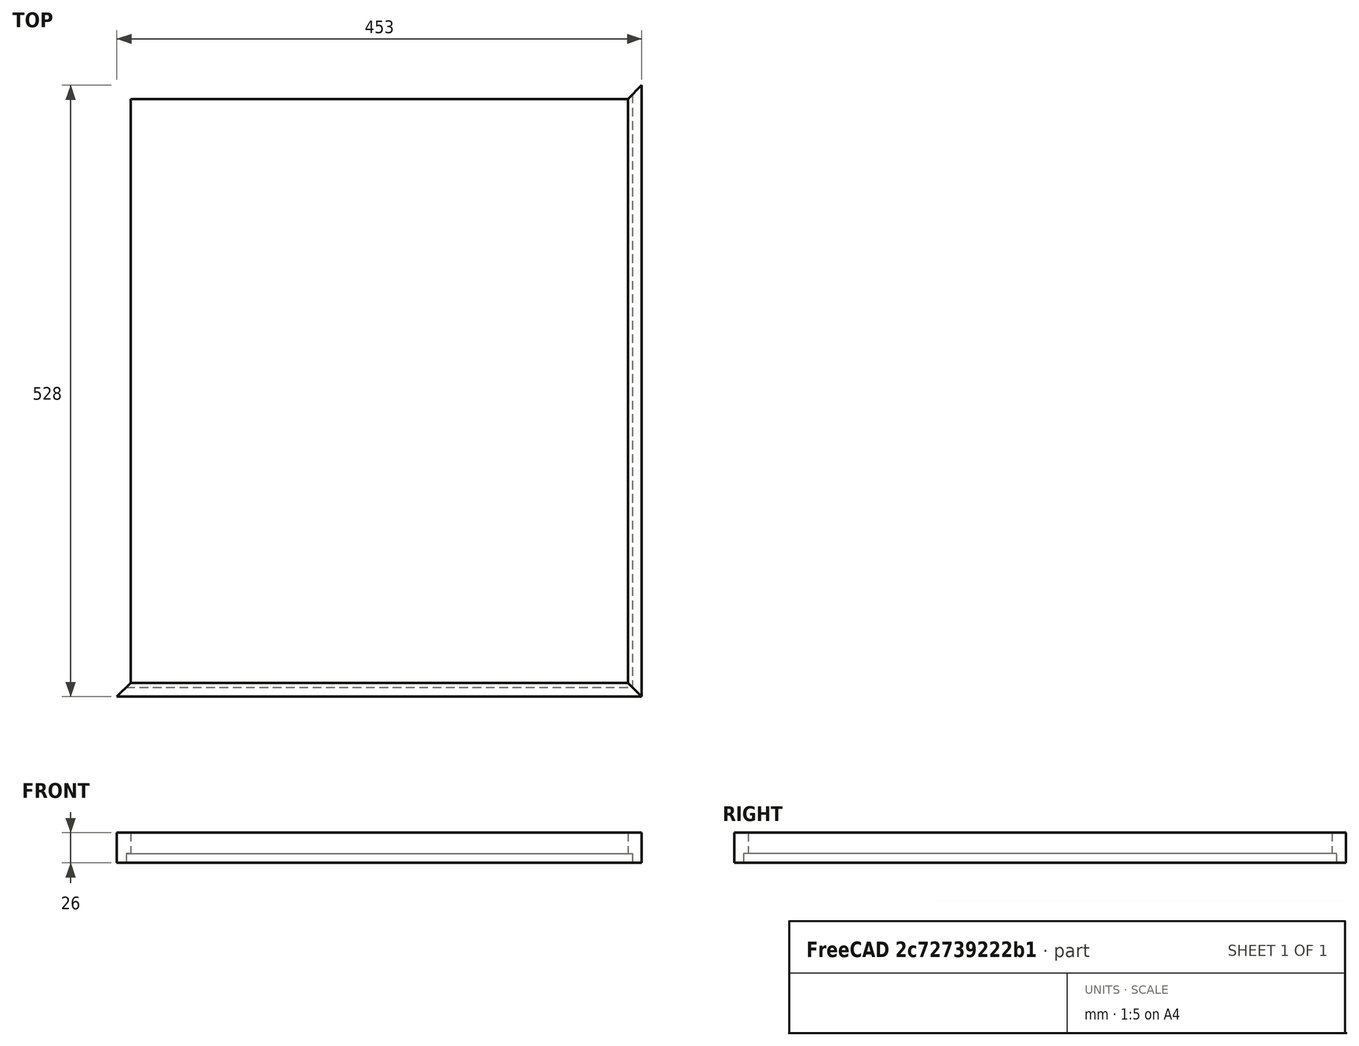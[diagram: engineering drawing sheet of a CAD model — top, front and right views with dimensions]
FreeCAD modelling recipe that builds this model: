
FCSTD DOCUMENT  (FreeCAD 0.19R)
Label: streha
License: All rights reserved
LicenseURL: http://en.wikipedia.org/wiki/All_rights_reserved
objects: Sketcher::SketchObject×8, PartDesign::CoordinateSystem×7, TechDraw::DrawProjGroupItem×6, TechDraw::DrawViewDimension×6, App::Link×5, PartDesign::Pocket×4, App::Part×4, App::DocumentObjectGroup×3, PartDesign::Pad×3, PartDesign::Body×3, TechDraw::DrawProjGroup×3, TechDraw::DrawRichAnno×3, App::FeaturePython×1, TechDraw::DrawSVGTemplate×1, TechDraw::DrawViewPart×1, TechDraw::DrawPage×1
note: 32 computed .brp shape members not serialized (recipe doc carries the construction recipe); baked Part::Feature solids carry a one-line shape summary decoded from their .brp

FEATURE [PartDesign::CoordinateSystem] LCS_Origin
  AttacherType = Attacher::AttachEngine3D
  MapMode = 2
  Support = -> [X_Axis]
FEATURE [App::FeaturePython] Variables  # WARN: FeaturePython — macro-defined, semantics opaque (R4)
  Type = App::PropertyContainer
  bottom_thickness = 18
  inner_depth = 450
  inner_width = 375
  wall_thickness = 27
FEATURE [App::DocumentObjectGroup] Constraints
FEATURE [App::DocumentObjectGroup] Configurations
FEATURE [PartDesign::CoordinateSystem] LCS_0004
  AttacherType = Attacher::AttachEngine3D
  MapMode = 2
  Support = -> [X_Axis005]
FEATURE [PartDesign::CoordinateSystem] LCS_0005
  AttacherType = Attacher::AttachEngine3D
  MapMode = 2
  Support = -> [X_Axis006]
FEATURE [Sketcher::SketchObject] Sketch003  label="Sketch004"
  FullyConstrained = true
  MapMode = 5
  Placement = pos=(0,0,0) rot=(1,0,0;1.5708rad)
  Support = -> [XZ_Plane006]
  expr: Constraints[12] = Variables.inner_width / 2 + Variables.wall_thickness
  sketch-geometry (6):
    g0: LineSegment StartX=214.5 StartY=0 StartZ=0 EndX=218.5 EndY=0 EndZ=0
    g1: LineSegment StartX=218.5 StartY=0 StartZ=0 EndX=218.5 EndY=-8 EndZ=0
    g2: LineSegment StartX=218.5 StartY=-8 StartZ=0 EndX=226.5 EndY=-8 EndZ=0
    g3: LineSegment StartX=226.5 StartY=-8 StartZ=0 EndX=226.5 EndY=25.6324 EndZ=0
    g4: LineSegment StartX=214.5 StartY=30 StartZ=0 EndX=214.5 EndY=0 EndZ=0
    g5: LineSegment StartX=214.5 StartY=30 StartZ=0 EndX=226.5 EndY=25.6324 EndZ=0
  constraints (18):
    c: Horizontal(g0)
    c: Coincident(g0,g1)
    c: Vertical(g1)
    c: Coincident(g1,g2)
    c: Horizontal(g2)
    c: Coincident(g2,g3)
    c: Vertical(g3)
    c: Coincident(g4,g0)
    c: Vertical(g4)
    c: DistanceX(g0,g0) = 4  'c'
    c: DistanceY(g1,g1) = 8  'd'
    c: Horizontal(g0,g-1)
    c: DistanceX(g-1,g0) = 214.5
    c: DistanceX(g0,g2) = 12  'a'
    c: DistanceY(g4,g4) = 30  'b'
    c: Coincident(g5,g4)
    c: Coincident(g5,g3)
    c: Angle(g5) = -0.349066  'e'
FEATURE [PartDesign::Pad] Pad002
  Direction = (1,1,1)
  Length = 700
  Length2 = 100
  Midplane = true
  Placement = pos=(0,0,0) rot=(1,0,0;1.5708rad)
  Profile = -> Sketch003
  Type = 0
FEATURE [Sketcher::SketchObject] Sketch004  label="Sketch005"
  ExternalGeometry = -> [Pad002]
  FullyConstrained = true
  MapMode = 5
  Support = -> [XY_Plane006]
  expr: Constraints[14] = Variables.inner_depth + 2 * Variables.wall_thickness
  sketch-geometry (8):
    g0: LineSegment StartX=226.5 StartY=-350 StartZ=0 EndX=226.5 EndY=-264 EndZ=0
    g1: LineSegment StartX=226.5 StartY=-264 StartZ=0 EndX=214.5 EndY=-252 EndZ=0
    g2: LineSegment StartX=214.5 StartY=-252 StartZ=0 EndX=214.5 EndY=-350 EndZ=0
    g3: LineSegment StartX=226.5 StartY=350 StartZ=0 EndX=226.5 EndY=264 EndZ=0
    g4: LineSegment StartX=226.5 StartY=264 StartZ=0 EndX=214.5 EndY=252 EndZ=0
    g5: LineSegment StartX=214.5 StartY=252 StartZ=0 EndX=214.5 EndY=350 EndZ=0
    g6: LineSegment StartX=214.5 StartY=-350 StartZ=0 EndX=226.5 EndY=-350 EndZ=0
    g7: LineSegment StartX=214.5 StartY=350 StartZ=0 EndX=226.5 EndY=350 EndZ=0
  constraints (20):
    c: Coincident(g0,g-4)
    c: Coincident(g1,g0)
    c: Coincident(g2,g1)
    c: Coincident(g2,g-4)
    c: Vertical(g2)
    c: Vertical(g0)
    c: Coincident(g-3,g3)
    c: Vertical(g3)
    c: Coincident(g3,g4)
    c: Coincident(g4,g5)
    c: Coincident(g5,g-3)
    c: Vertical(g5)
    c: Equal(g4,g1)
    c: Equal(g5,g2)
    c: DistanceY(g1,g4) = 504
    c: Coincident(g6,g2)
    c: Coincident(g6,g0)
    c: Coincident(g7,g5)
    c: Coincident(g7,g3)
    c: Perpendicular(g4,g1)
FEATURE [PartDesign::Pocket] Pocket001
  BaseFeature = -> Pad002
  Length = 41
  Length2 = 100
  Midplane = true
  Placement = pos=(0,0,0) rot=(1,0,0;1.5708rad)
  Profile = -> Sketch004
  Type = 1
FEATURE [PartDesign::CoordinateSystem] LCS_0006
  AttacherType = Attacher::AttachEngine3D
  MapMode = 2
  Support = -> [X_Axis007]
FEATURE [PartDesign::CoordinateSystem] LCS_0007
  AttacherType = Attacher::AttachEngine3D
  MapMode = 2
  Support = -> [X_Axis008]
FEATURE [Sketcher::SketchObject] Sketch005  label="Sketch006"
  FullyConstrained = true
  MapMode = 5
  Placement = pos=(0,0,0) rot=(0.57735,0.57735,0.57735;2.0944rad)
  Support = -> [YZ_Plane008]
  expr: Constraints[17] = Variables.inner_depth / 2 + Variables.wall_thickness
  sketch-geometry (6):
    g0: LineSegment StartX=-252 StartY=0 StartZ=0 EndX=-252 EndY=30 EndZ=0
    g1: LineSegment StartX=-264 StartY=25.6324 StartZ=0 EndX=-264 EndY=-8 EndZ=0
    g2: LineSegment StartX=-264 StartY=-8 StartZ=0 EndX=-256 EndY=-8 EndZ=0
    g3: LineSegment StartX=-256 StartY=-8 StartZ=0 EndX=-256 EndY=0 EndZ=0
    g4: LineSegment StartX=-256 StartY=0 StartZ=0 EndX=-252 EndY=0 EndZ=0
    g5: LineSegment StartX=-264 StartY=25.6324 StartZ=0 EndX=-252 EndY=30 EndZ=0
  constraints (18):
    c: Vertical(g0)
    c: Vertical(g1)
    c: Coincident(g1,g2)
    c: Horizontal(g2)
    c: Coincident(g2,g3)
    c: Vertical(g3)
    c: Coincident(g3,g4)
    c: Coincident(g4,g0)
    c: Horizontal(g4)
    c: Horizontal(g0,g-1)
    c: DistanceX(g4,g4) = 4
    c: DistanceY(g3,g3) = 8
    c: DistanceX(g1,g0) = 12
    c: DistanceY(g0,g0) = 30
    c: Coincident(g5,g1)
    c: Coincident(g5,g0)
    c: Angle(g5) = 0.349066
    c: DistanceX(g0,g-1) = 252
FEATURE [PartDesign::Pad] Pad003
  Direction = (1,1,1)
  Length = 700
  Length2 = 100
  Midplane = true
  Placement = pos=(0,0,0) rot=(0.57735,0.57735,0.57735;2.0944rad)
  Profile = -> Sketch005
  Type = 0
FEATURE [Sketcher::SketchObject] Sketch006  label="Sketch007"
  ExternalGeometry = -> [Pad003]
  FullyConstrained = true
  MapMode = 5
  Support = -> [XY_Plane008]
  expr: Constraints[19] = Variables.inner_width + 2 * Variables.wall_thickness
  sketch-geometry (8):
    g0: LineSegment StartX=-350 StartY=-264 StartZ=0 EndX=-350 EndY=-252 EndZ=0
    g1: LineSegment StartX=-350 StartY=-252 StartZ=0 EndX=-214.5 EndY=-252 EndZ=0
    g2: LineSegment StartX=-214.5 StartY=-252 StartZ=0 EndX=-226.5 EndY=-264 EndZ=0
    g3: LineSegment StartX=-226.5 StartY=-264 StartZ=0 EndX=-350 EndY=-264 EndZ=0
    g4: LineSegment StartX=350 StartY=-264 StartZ=0 EndX=350 EndY=-252 EndZ=0
    g5: LineSegment StartX=350 StartY=-252 StartZ=0 EndX=214.5 EndY=-252 EndZ=0
    g6: LineSegment StartX=214.5 StartY=-252 StartZ=0 EndX=226.5 EndY=-264 EndZ=0
    g7: LineSegment StartX=226.5 StartY=-264 StartZ=0 EndX=350 EndY=-264 EndZ=0
  constraints (20):
    c: Coincident(g-3,g0)
    c: Coincident(g0,g-3)
    c: Coincident(g0,g1)
    c: Coincident(g1,g2)
    c: Coincident(g2,g3)
    c: Coincident(g3,g0)
    c: Coincident(g-4,g4)
    c: Coincident(g4,g-4)
    c: Coincident(g4,g5)
    c: Coincident(g5,g6)
    c: Coincident(g6,g7)
    c: Coincident(g7,g4)
    c: Perpendicular(g2,g6)
    c: Equal(g2,g6)
    c: Equal(g1,g5)
    c: Horizontal(g1)
    c: Horizontal(g3)
    c: Horizontal(g7)
    c: Horizontal(g5)
    c: DistanceX(g1,g5) = 429
FEATURE [PartDesign::Pocket] Pocket002
  BaseFeature = -> Pad003
  Length = 5
  Length2 = 100
  Midplane = true
  Placement = pos=(0,0,0) rot=(0.57735,0.57735,0.57735;2.0944rad)
  Profile = -> Sketch006
  Type = 1
FEATURE [App::Link] Slat003  label="slat_right"
  AssemblyType = Part::Link
  AttachedBy = #LCS_0004
  AttachedTo = Parent Assembly#LCS_Origin
  LinkedObject = -> Slat
  SolverId = Asm4EE
  expr: Placement = LCS_Origin.Placement * AttachmentOffset * LCS_0004.Placement ^ -1
FEATURE [App::Link] Slat2001  label="slat_front"
  AssemblyType = Part::Link
  AttachedBy = #LCS_0006
  AttachedTo = Parent Assembly#LCS_Origin
  LinkedObject = -> Slat2
  SolverId = Asm4EE
  expr: Placement = LCS_Origin.Placement * AttachmentOffset * LCS_0006.Placement ^ -1
FEATURE [App::Link] Slat2002  label="slat_left"
  AssemblyType = Part::Link
  AttachedBy = #LCS_0004
  AttachedTo = Parent Assembly#LCS_Origin
  AttachmentOffset = pos=(0,0,0) rot=(0,0,1;3.14159rad)
  LinkPlacement = pos=(0,0,0) rot=(0,0,1;3.14159rad)
  LinkedObject = -> Slat
  Placement = pos=(0,0,0) rot=(0,0,1;3.14159rad)
  SolverId = Asm4EE
  expr: Placement = LCS_Origin.Placement * AttachmentOffset * LCS_0004.Placement ^ -1
FEATURE [App::Link] Slat2003  label="slat_rear"
  AssemblyType = Part::Link
  AttachedBy = #LCS_0006
  AttachedTo = Parent Assembly#LCS_Origin
  AttachmentOffset = pos=(0,0,0) rot=(0,0,1;3.14159rad)
  LinkPlacement = pos=(0,0,0) rot=(0,0,1;3.14159rad)
  LinkedObject = -> Slat2
  Placement = pos=(0,0,0) rot=(0,0,1;3.14159rad)
  SolverId = Asm4EE
  expr: Placement = LCS_Origin.Placement * AttachmentOffset * LCS_0006.Placement ^ -1
FEATURE [TechDraw::DrawSVGTemplate] Template001
  EditableTexts = AVTOR=Brane Borštnik; AVTOR_2=Risal: Janez Paternoster; DATUM=6.5.2022; MATERIAL=Les, smreka; MERILO=1:5; NAZIV=Streha; NAZIV_2=Dadant-Blatt panj; STRAN=Stran 1/1; VIR=https://github.com/<owner>/Dadant-Blatt
  Height = 297
  Orientation = 0
  Width = 210
FEATURE [PartDesign::CoordinateSystem] LCS_0010
  AttacherType = Attacher::AttachEngine3D
  MapMode = 2
  Support = -> [X_Axis011]
FEATURE [PartDesign::CoordinateSystem] LCS_0011
  AttacherType = Attacher::AttachEngine3D
  MapMode = 2
  Support = -> [X_Axis012]
FEATURE [Sketcher::SketchObject] Sketch007  label="Sketch008"
  FullyConstrained = true
  MapMode = 5
  Support = -> [XY_Plane012]
  expr: Constraints[12] = Variables.inner_depth + Variables.wall_thickness * 2
  expr: Constraints[11] = Variables.inner_width + Variables.wall_thickness * 2
  sketch-geometry (5):
    g0: LineSegment StartX=214.5 StartY=252 StartZ=0 EndX=-214.5 EndY=252 EndZ=0
    g1: LineSegment StartX=-214.5 StartY=252 StartZ=0 EndX=-214.5 EndY=-252 EndZ=0
    g2: LineSegment StartX=-214.5 StartY=-252 StartZ=0 EndX=214.5 EndY=-252 EndZ=0
    g3: LineSegment StartX=214.5 StartY=-252 StartZ=0 EndX=214.5 EndY=252 EndZ=0
    g4: Circle CenterX=0 CenterY=0 CenterZ=0 NormalX=0 NormalY=0 NormalZ=1 AngleXU=0 Radius=330.929
  constraints (14):
    c: Coincident(g0,g1)
    c: Coincident(g1,g2)
    c: Coincident(g2,g3)
    c: Coincident(g3,g0)
    c: Equal(g0,g2)
    c: PointOnObject(g0,g4)
    c: PointOnObject(g1,g4)
    c: PointOnObject(g2,g4)
    c: PointOnObject(g3,g4)
    c: Coincident(g4,g-1)
    c: Horizontal(g2)
    c: DistanceX(g0,g0) = 429
    c: DistanceY(g3,g3) = 504
    c: Vertical(g1)
FEATURE [PartDesign::Pad] Pad004
  Direction = (1,1,1)
  Length = 18
  Length2 = 100
  Profile = -> Sketch007
  Type = 0
  expr: Length = Variables.bottom_thickness
FEATURE [App::Link] bottom001
  AssemblyType = Part::Link
  AttachedBy = #LCS_0010
  AttachedTo = Parent Assembly#LCS_Origin
  LinkedObject = -> bottom
  SolverId = Asm4EE
  expr: Placement = LCS_Origin.Placement * AttachmentOffset * LCS_0010.Placement ^ -1
FEATURE [App::Part] Assembly
  AssemblyType = Part::Link
  Group = -> [LCS_Origin,Constraints,Configurations,Slat003,Slat2001,Slat2002,Slat2003,bottom001]
  LabelDocUser = naklada
  LabelPartUser = Assembly
  Origin = -> Origin
  Type = Assembly
FEATURE [Sketcher::SketchObject] Sketch
  ExternalGeometry = -> [Pocket001]
  FullyConstrained = true
  MapMode = 5
  Placement = pos=(0,0,0) rot=(1,0,0;1.5708rad)
  Support = -> [XZ_Plane006]
  expr: Constraints[10] = Variables.bottom_thickness
  sketch-geometry (4):
    g0: LineSegment StartX=214.5 StartY=18 StartZ=0 EndX=226.5 EndY=18 EndZ=0
    g1: LineSegment StartX=226.5 StartY=18 StartZ=0 EndX=226.5 EndY=30 EndZ=0
    g2: LineSegment StartX=226.5 StartY=30 StartZ=0 EndX=214.5 EndY=30 EndZ=0
    g3: LineSegment StartX=214.5 StartY=30 StartZ=0 EndX=214.5 EndY=18 EndZ=0
  constraints (11):
    c: Coincident(g0,g1)
    c: Coincident(g1,g2)
    c: Coincident(g2,g3)
    c: Coincident(g3,g0)
    c: Horizontal(g0)
    c: Horizontal(g2)
    c: Vertical(g1)
    c: Vertical(g3)
    c: Coincident(g2,g-3)
    c: PointOnObject(g-3,g1)
    c: DistanceY(g-1,g0) = 18
FEATURE [PartDesign::Pocket] Pocket
  BaseFeature = -> Pocket001
  Length = 5
  Length2 = 100
  Midplane = true
  Placement = pos=(0,0,0) rot=(1,0,0;1.5708rad)
  Profile = -> Sketch
  Type = 1
FEATURE [PartDesign::Body] Body_3
  Group = -> [LCS_0005,Sketch003,Pad002,Sketch004,Pocket001,Sketch,Pocket]
  Origin = -> Origin006
  Tip = -> Pocket
FEATURE [App::Part] Slat  label="slat_side"
  Group = -> [LCS_0004,Body_3]
  Origin = -> Origin005
FEATURE [TechDraw::DrawProjGroupItem] ProjItem004  label="Front002"
  CoarseView = false
  Direction = (0,0,1)
  Focus = 100
  HardHidden = false
  IsoCount = 0
  IsoHidden = false
  IsoVisible = false
  LockPosition = true
  Perspective = false
  Rotation = 0
  RotationVector = (1,0,0)
  Scale = 0.2
  ScaleType = 2
  SeamHidden = false
  SeamVisible = true
  SmoothHidden = false
  SmoothVisible = true
  Source = -> [Slat]
  Type = 0
  X = 0
  XDirection = (1e-16,1,0)
  Y = 0
FEATURE [TechDraw::DrawProjGroupItem] ProjItem005  label="Left002"
  CoarseView = false
  Direction = (-1e-16,-1,1e-16)
  Focus = 100
  HardHidden = false
  IsoCount = 0
  IsoHidden = false
  IsoVisible = false
  LockPosition = false
  Perspective = false
  Rotation = 0
  RotationVector = (1,0,0)
  Scale = 0.2
  ScaleType = 2
  SeamHidden = false
  SeamVisible = true
  SmoothHidden = false
  SmoothVisible = true
  Source = -> [Slat]
  Type = 1
  X = 65.4
  XDirection = (0,1e-16,1)
  Y = 0
FEATURE [TechDraw::DrawProjGroup] ProjGroup002
  Anchor = -> ProjItem004
  AutoDistribute = true
  LockPosition = false
  ProjectionType = 0
  Rotation = 0
  Scale = 0.2
  ScaleType = 0
  Source = -> [Slat]
  Views = -> [ProjItem004,ProjItem005]
  X = 80.5609
  Y = 178.206
  spacingX = 10
  spacingY = 15
FEATURE [TechDraw::DrawViewDimension] Dimension023
  Arbitrary = false
  ArbitraryTolerances = false
  EqualTolerance = true
  FormatSpec = %.6g
  FormatSpecOverTolerance = %+.6g
  FormatSpecUnderTolerance = %+.6g
  Inverted = false
  LockPosition = false
  MeasureType = 1
  OverTolerance = 0
  References2D = -> [ProjItem004]
  Rotation = 0
  Scale = 0.2
  ScaleType = 0
  TheoreticalExact = false
  Type = 1
  UnderTolerance = 0
  X = -0.440729
  Y = 11.1164
FEATURE [TechDraw::DrawRichAnno] RichTextAnnotation
  AnnoParent = -> ProjItem004
  AnnoText = <!DOCTYPE HTML PUBLIC "-//W3C//DTD HTML 4.0//EN" "http://www.w3.org/TR/REC-html40/strict.dtd">\n<html><head><meta name="qrichtext" content="1" /><style type="text/css">\np, li { white-space: pre-wrap; }\n</style></head><body style=" font-family:'Ubuntu'; font-size:11pt; font-weight:400; font-style:normal;">\n<p style=" margin-top:0px; margin-bottom:0px; margin-left:0px; margin-right:0px; -qt-block-indent:0; text-indent:0px;"><span style=" font-size:10pt;">2 kom</span></p></body></html>
  LockPosition = false
  MaxWidth = -1
  Rotation = 0
  Scale = 0.2
  ScaleType = 0
  ShowFrame = false
  X = 56.6723
  Y = -5.45734
FEATURE [Sketcher::SketchObject] Sketch008  label="Sketch009"
  ExternalGeometry = -> [Pocket002]
  FullyConstrained = true
  MapMode = 5
  Placement = pos=(0,0,0) rot=(0.57735,0.57735,0.57735;2.0944rad)
  Support = -> [YZ_Plane008]
  expr: Constraints[10] = Variables.bottom_thickness
  sketch-geometry (4):
    g0: LineSegment StartX=-264 StartY=30 StartZ=0 EndX=-252 EndY=30 EndZ=0
    g1: LineSegment StartX=-252 StartY=30 StartZ=0 EndX=-252 EndY=18 EndZ=0
    g2: LineSegment StartX=-252 StartY=18 StartZ=0 EndX=-264 EndY=18 EndZ=0
    g3: LineSegment StartX=-264 StartY=18 StartZ=0 EndX=-264 EndY=30 EndZ=0
  constraints (11):
    c: Coincident(g0,g1)
    c: Coincident(g1,g2)
    c: Coincident(g2,g3)
    c: Coincident(g3,g0)
    c: Horizontal(g0)
    c: Horizontal(g2)
    c: Vertical(g1)
    c: Vertical(g3)
    c: Coincident(g0,g-3)
    c: PointOnObject(g-3,g3)
    c: DistanceY(g-1,g1) = 18
FEATURE [PartDesign::Pocket] Pocket003
  BaseFeature = -> Pocket002
  Length = 5
  Length2 = 100
  Midplane = true
  Placement = pos=(0,0,0) rot=(0.57735,0.57735,0.57735;2.0944rad)
  Profile = -> Sketch008
  Type = 1
FEATURE [PartDesign::Body] Body_4
  Group = -> [LCS_0007,Sketch005,Pad003,Sketch006,Pocket002,Sketch008,Pocket003]
  Origin = -> Origin008
  Tip = -> Pocket003
FEATURE [App::Part] Slat2  label="slat_front_rear"
  Group = -> [LCS_0006,Body_4]
  Origin = -> Origin007
FEATURE [TechDraw::DrawProjGroupItem] ProjItem006  label="Front003"
  CoarseView = false
  Direction = (0,0,1)
  Focus = 100
  HardHidden = false
  IsoCount = 0
  IsoHidden = false
  IsoVisible = false
  LockPosition = true
  Perspective = false
  Rotation = 0
  RotationVector = (1,0,0)
  Scale = 0.2
  ScaleType = 2
  SeamHidden = false
  SeamVisible = true
  SmoothHidden = false
  SmoothVisible = true
  Source = -> [Slat2]
  Type = 0
  X = 0
  XDirection = (1,0,0)
  Y = 0
FEATURE [TechDraw::DrawProjGroupItem] ProjItem007  label="Left003"
  CoarseView = false
  Direction = (-1,0,1e-16)
  Focus = 100
  HardHidden = false
  IsoCount = 0
  IsoHidden = false
  IsoVisible = false
  LockPosition = false
  Perspective = false
  Rotation = 0
  RotationVector = (1,0,0)
  Scale = 0.2
  ScaleType = 2
  SeamHidden = false
  SeamVisible = true
  SmoothHidden = false
  SmoothVisible = true
  Source = -> [Slat2]
  Type = 1
  X = 57.9
  XDirection = (1e-16,0,1)
  Y = 0
FEATURE [TechDraw::DrawProjGroup] ProjGroup003
  Anchor = -> ProjItem006
  AutoDistribute = true
  LockPosition = false
  ProjectionType = 0
  Rotation = 0
  Scale = 0.2
  ScaleType = 0
  Source = -> [Slat2]
  Views = -> [ProjItem006,ProjItem007]
  X = 76.6949
  Y = 154.558
  spacingX = 10
  spacingY = 15
FEATURE [TechDraw::DrawViewDimension] Dimension024
  Arbitrary = false
  ArbitraryTolerances = false
  EqualTolerance = true
  FormatSpec = %.6g
  FormatSpecOverTolerance = %+.6g
  FormatSpecUnderTolerance = %+.6g
  Inverted = false
  LockPosition = false
  MeasureType = 1
  OverTolerance = 0
  References2D = -> [ProjItem006]
  Rotation = 0
  Scale = 0.2
  ScaleType = 0
  TheoreticalExact = false
  Type = 1
  UnderTolerance = 0
  X = 0
  Y = 12.659
FEATURE [TechDraw::DrawRichAnno] RichTextAnnotation006
  AnnoParent = -> ProjItem006
  AnnoText = <!DOCTYPE HTML PUBLIC "-//W3C//DTD HTML 4.0//EN" "http://www.w3.org/TR/REC-html40/strict.dtd">\n<html><head><meta name="qrichtext" content="1" /><style type="text/css">\np, li { white-space: pre-wrap; }\n</style></head><body style=" font-family:'Ubuntu'; font-size:11pt; font-weight:400; font-style:normal;">\n<p style=" margin-top:0px; margin-bottom:0px; margin-left:0px; margin-right:0px; -qt-block-indent:0; text-indent:0px;"><span style=" font-size:10pt;">2 kom</span></p></body></html>
  LockPosition = false
  MaxWidth = -1
  Rotation = 0
  Scale = 0.2
  ScaleType = 0
  ShowFrame = false
  X = 49.7457
  Y = -4.61775
FEATURE [TechDraw::DrawViewPart] View
  CoarseView = false
  Direction = (0.577,-0.577,0.577)
  Focus = 100
  HardHidden = false
  IsoCount = 0
  IsoHidden = false
  IsoVisible = false
  LockPosition = false
  Perspective = false
  Rotation = 0
  Scale = 0.2
  ScaleType = 0
  SeamHidden = false
  SeamVisible = true
  SmoothHidden = false
  SmoothVisible = true
  Source = -> [Assembly]
  X = 103.749
  XDirection = (0.707,0.707,0)
  Y = 245.275
FEATURE [TechDraw::DrawRichAnno] RichTextAnnotation007
  AnnoParent = -> View
  AnnoText = <!DOCTYPE HTML PUBLIC "-//W3C//DTD HTML 4.0//EN" "http://www.w3.org/TR/REC-html40/strict.dtd">\n<html><head><meta name="qrichtext" content="1" /><style type="text/css">\np, li { white-space: pre-wrap; }\n</style></head><body style=" font-family:'Ubuntu'; font-size:11pt; font-weight:400; font-style:normal;">\n<p style=" margin-top:0px; margin-bottom:0px; margin-left:0px; margin-right:0px; -qt-block-indent:0; text-indent:0px;"><span style=" font-size:10pt;">Zgoraj prekrito s pločevino.</span></p></body></html>
  LockPosition = false
  MaxWidth = -1
  Rotation = 0
  Scale = 0.2
  ScaleType = 0
  ShowFrame = false
  X = 0
  Y = 0
FEATURE [Sketcher::SketchObject] Sketch009  label="Sketch010"
  FullyConstrained = true
  MapMode = 5
  Support = -> [XY_Plane012]
  expr: Constraints[9] = Variables.inner_depth
  expr: Constraints[8] = Variables.inner_width
  sketch-geometry (4):
    g0: LineSegment StartX=-187.5 StartY=-225 StartZ=0 EndX=187.5 EndY=-225 EndZ=0
    g1: LineSegment StartX=187.5 StartY=-225 StartZ=0 EndX=187.5 EndY=225 EndZ=0
    g2: LineSegment StartX=187.5 StartY=225 StartZ=0 EndX=-187.5 EndY=225 EndZ=0
    g3: LineSegment StartX=-187.5 StartY=225 StartZ=0 EndX=-187.5 EndY=-225 EndZ=0
  constraints (10):
    c: Coincident(g0,g1)
    c: Coincident(g1,g2)
    c: Coincident(g2,g3)
    c: Coincident(g3,g0)
    c: Horizontal(g2)
    c: Vertical(g3)
    c: Symmetric(g0,g0,g-2)
    c: Symmetric(g0,g1,g-1)
    c: DistanceX(g2,g2) = 375
    c: DistanceY(g3,g3) = 450
FEATURE [PartDesign::Body] Body_5
  Group = -> [LCS_0011,Sketch007,Pad004,Sketch009]
  Origin = -> Origin012
  Tip = -> Pad004
FEATURE [App::Part] bottom
  Group = -> [LCS_0010,Body_5]
  Origin = -> Origin011
FEATURE [App::DocumentObjectGroup] Parts
  Group = -> [Slat,Slat2,bottom]
FEATURE [TechDraw::DrawProjGroupItem] ProjItem  label="Front"
  CoarseView = false
  Direction = (0,0,-1)
  Focus = 100
  HardHidden = false
  IsoCount = 0
  IsoHidden = false
  IsoVisible = false
  LockPosition = true
  Perspective = false
  Rotation = 0
  RotationVector = (0,1,0)
  ScaleType = 2
  SeamHidden = false
  SeamVisible = true
  SmoothHidden = false
  SmoothVisible = true
  Source = -> [Body_5,Sketch009]
  Type = 0
  X = 0
  XDirection = (0,1,0)
  Y = 0
FEATURE [TechDraw::DrawProjGroupItem] ProjItem015  label="Left"
  CoarseView = false
  Direction = (0,-1,-1e-16)
  Focus = 100
  HardHidden = false
  IsoCount = 0
  IsoHidden = false
  IsoVisible = false
  LockPosition = false
  Perspective = false
  Rotation = 0
  RotationVector = (1,0,0)
  ScaleType = 2
  SeamHidden = false
  SeamVisible = true
  SmoothHidden = false
  SmoothVisible = true
  Source = -> [Body_5,Sketch009]
  Type = 1
  X = 67.2
  XDirection = (0,1e-16,-1)
  Y = 0
FEATURE [TechDraw::DrawProjGroup] ProjGroup
  Anchor = -> ProjItem
  AutoDistribute = true
  LockPosition = false
  ProjectionType = 0
  Rotation = 0
  Scale = 0.2
  ScaleType = 0
  Source = -> [Body_5,Sketch009]
  Views = -> [ProjItem,ProjItem015]
  X = 84.2366
  Y = 78.2168
  spacingX = 15
  spacingY = 15
FEATURE [TechDraw::DrawViewDimension] Dimension
  Arbitrary = false
  ArbitraryTolerances = false
  EqualTolerance = true
  FormatSpec = %.6g
  FormatSpecOverTolerance = %+.6g
  FormatSpecUnderTolerance = %+.6g
  Inverted = false
  LockPosition = false
  MeasureType = 1
  OverTolerance = 0
  References2D = -> [ProjItem]
  Rotation = 0
  Scale = 0.2
  ScaleType = 0
  TheoreticalExact = false
  Type = 1
  UnderTolerance = 0
  X = 1.31124
  Y = 64.4419
FEATURE [TechDraw::DrawViewDimension] Dimension025
  Arbitrary = false
  ArbitraryTolerances = false
  EqualTolerance = true
  FormatSpec = %.6g
  FormatSpecOverTolerance = %+.6g
  FormatSpecUnderTolerance = %+.6g
  Inverted = false
  LockPosition = false
  MeasureType = 1
  OverTolerance = 0
  References2D = -> [ProjItem]
  Rotation = 0
  Scale = 0.2
  ScaleType = 0
  TheoreticalExact = false
  Type = 2
  UnderTolerance = 0
  X = -60.328
  Y = 0.936603
FEATURE [TechDraw::DrawViewDimension] Dimension026
  Arbitrary = false
  ArbitraryTolerances = false
  EqualTolerance = true
  FormatSpec = %.6g
  FormatSpecOverTolerance = %+.6g
  FormatSpecUnderTolerance = %+.6g
  Inverted = false
  LockPosition = false
  MeasureType = 1
  OverTolerance = 0
  References2D = -> [ProjItem015]
  Rotation = 0
  Scale = 0.2
  ScaleType = 0
  TheoreticalExact = false
  Type = 1
  UnderTolerance = 0
  X = 9.92799
  Y = 63.3179
FEATURE [TechDraw::DrawViewDimension] Dimension027
  Arbitrary = false
  ArbitraryTolerances = false
  EqualTolerance = true
  FormatSpec = (debelina stene panja = %.6g)
  FormatSpecOverTolerance = %+.6g
  FormatSpecUnderTolerance = %+.6g
  Inverted = false
  LockPosition = false
  MeasureType = 1
  OverTolerance = 0
  References2D = -> [ProjItem]
  Rotation = 0
  Scale = 0.2
  ScaleType = 0
  TheoreticalExact = false
  Type = 1
  UnderTolerance = 0
  X = 9.29929
  Y = 54.0617
FEATURE [TechDraw::DrawPage] Page001  label="Page1"
  KeepUpdated = true
  NextBalloonIndex = 1
  ProjectionType = 0
  Scale = 0.2
  Template = -> Template001
  Views = -> [ProjGroup002,ProjGroup003,Dimension023,Dimension024,RichTextAnnotation,RichTextAnnotation006,View,RichTextAnnotation007,ProjGroup,Dimension,Dimension025,Dimension026,Dimension027]
